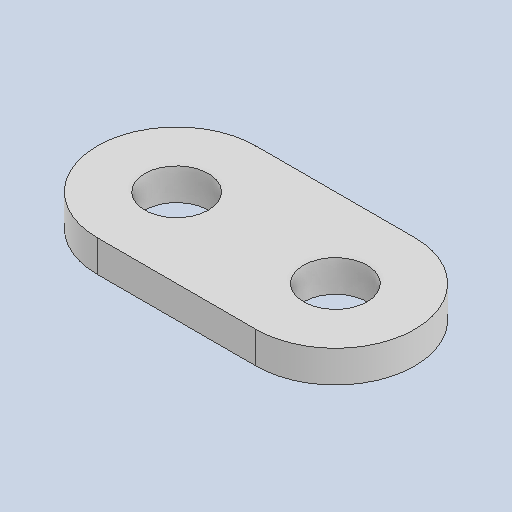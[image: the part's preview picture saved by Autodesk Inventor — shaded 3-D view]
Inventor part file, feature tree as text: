
AUTODESK INVENTOR PART (.ipt)
format: ipt  version: 2023 (Build 270158000, 158)  size: 226,816 bytes
history: native  units: mm
features: extrude x1, sketch x1
ambient origin geometry x8: Origin, YZ Plane, XZ Plane, XY Plane, X Axis, Y Axis, Z Axis, Center Point
bodies: Solid1 (feature_tree)
feature tree (2):
  extrude  "Extrusion1"  Depth=2.0mm
  sketch  "Sketch1"  dims[d0=10.0mm d1=4.0mm d3=20.0mm d4=2.0mm d5=0.0mm]
